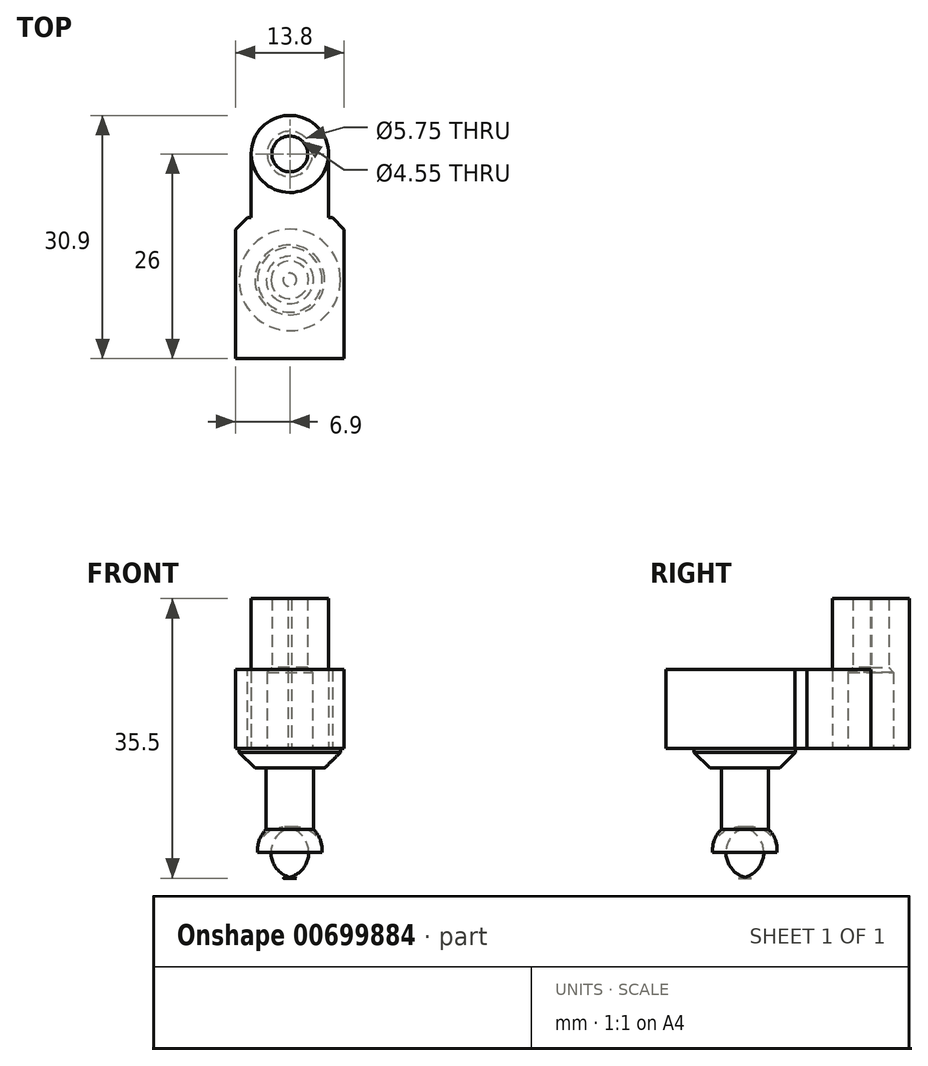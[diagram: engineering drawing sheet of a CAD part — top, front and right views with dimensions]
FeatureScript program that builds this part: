
annotation { "Feature Type Name" : "Feature", "Feature Type Description" : "" }
export const myFeature = defineFeature(function(context is Context, id is Id, definition is map)
    precondition{}
    {
        {
            var Q0;
            Q0=qCreatedBy(makeId("Top.planeOp"),FACE);
            var sketch = newSketch(context, id + "F0", { "sketchPlane" : qUnion([Q0])});
            skLineSegment(sketch, "E0.bottom", {"start": v(0, 0) * mm, "end": v(13.8, 0) * mm});
            skLineSegment(sketch, "E0.top", {"start": v(0, 17.9) * mm, "end": v(13.8, 17.9) * mm});
            skLineSegment(sketch, "E0.left", {"start": v(0, 0) * mm, "end": v(0, 17.9) * mm});
            skLineSegment(sketch, "E0.right", {"start": v(13.8, 0) * mm, "end": v(13.8, 17.9) * mm});
            skLineSegment(sketch, "E1", {"start": v(2, 17.9) * mm, "end": v(2, 26.15) * mm});
            skLineSegment(sketch, "E2", {"start": v(6.74, 30.9) * mm, "end": v(7.12, 30.9) * mm});
            skLineSegment(sketch, "E3", {"start": v(11.8, 26.21) * mm, "end": v(11.8, 17.9) * mm});
            skCircle(sketch, "E4", {"center": v(6.9, 26) * mm, "radius": 2.28 * mm});
            skCircle(sketch, "E5", {"center": v(6.9, 26) * mm, "radius": 4.9 * mm});
            skPoint(sketch, "E6.visualSharp", {"position": v(2, 30.9) * mm});
            skArc(sketch, "E6.filletArc", {"start": v(6.74, 30.9) * mm, "mid": v(3.39, 29.5) * mm, "end": v(2, 26.15) * mm});
            skPoint(sketch, "E7.visualSharp", {"position": v(11.8, 30.9) * mm});
            skArc(sketch, "E7.filletArc", {"start": v(11.8, 26.21) * mm, "mid": v(10.43, 29.52) * mm, "end": v(7.12, 30.9) * mm});
            skCircle(sketch, "E8", {"center": v(6.9, 10) * mm, "radius": 3 * mm});
            skCircle(sketch, "E9", {"center": v(6.9, 10) * mm, "radius": 4.1 * mm});
            skCircle(sketch, "E10", {"center": v(6.9, 10) * mm, "radius": 6.44 * mm});
            skCircle(sketch, "E11", {"center": v(6.9, 26) * mm, "radius": 2.88 * mm});
            skSolve(sketch);
        }
        {
            var Q0;
            {var subQ7=sQuery(id+"F0.wireOp",EDGE,"E2");Q0=makeQuery(id+"F0.imprint","IMPRINT",FACE,{"disambiguationData":[TD([[makeQuery(id+"F0.imprint","IMPRINT",EDGE,{"derivedFrom":subQ7}),-1.0]])]});}
            extrude(context, id + "F1", {"entities" : qUnion([Q0]), "depth" : 19 * mm, "offsetDistance" : 25 * mm});
        }
        {
            var Q0;
            Q0=makeQuery(id+"F0.imprint","IMPRINT",FACE,{"disambiguationData":[TD([[makeQuery(id+"F0.imprint","IMPRINT",EDGE,{"derivedFrom":sQuery(id+"F0.wireOp",EDGE,"E8")}),1.0]])]});
            extrude(context, id + "F2", {"entities" : qUnion([Q0]), "depth" : -16.5 * mm, "offsetDistance" : 25 * mm});
        }
        {
            var Q0;
            Q0=makeQuery(id+"F0.imprint","IMPRINT",FACE,{"disambiguationData":[TD([[makeQuery(id+"F0.imprint","IMPRINT",EDGE,{"derivedFrom":sQuery(id+"F0.wireOp",EDGE,"E8")}),-1.0]])]});
            extrude(context, id + "F3", {"entities" : qUnion([Q0]), "operationType" : NewBodyOperationType.ADD, "depth" : -16.5 * mm, "offsetDistance" : 25 * mm, "hasSecondDirection" : true, "secondDirectionOppositeDirection" : true, "secondDirectionDepth" : 10.3 * mm});
        }
        {
            var Q0;
            Q0=makeQuery(id+"F0.imprint","IMPRINT",FACE,{"disambiguationData":[TD([[makeQuery(id+"F0.imprint","IMPRINT",EDGE,{"derivedFrom":sQuery(id+"F0.wireOp",EDGE,"E9")}),-1.0]])]});
            var Q1;
            Q1=makeQuery(id+"F0.imprint","IMPRINT",FACE,{"disambiguationData":[TD([[makeQuery(id+"F0.imprint","IMPRINT",EDGE,{"derivedFrom":sQuery(id+"F0.wireOp",EDGE,"E8")}),-1.0]])]});
            extrude(context, id + "F4", {"entities" : qUnion([Q0, Q1]), "operationType" : NewBodyOperationType.ADD, "depth" : -2.5 * mm, "offsetDistance" : 25 * mm});
        }
        {
            var Q0;
            {var subQ0=sQuery(id+"F0.wireOp",EDGE,"E1");var subQ1=sQuery(id+"F0.wireOp",EDGE,"E0.top");var subQ2=makeQuery(id+"F0.imprint","INTERSECT",VERTEX,{"derivedFrom":[subQ1,subQ0]});Q0=makeQuery(id+"F0.imprint","IMPRINT",FACE,{"disambiguationData":[TD([[makeQuery(id+"F0.imprint","IMPRINT",EDGE,{"disambiguationData":[TD([[subQ2,-1.0]])],"derivedFrom":subQ1}),1.0]])]});}
            var Q1;
            Q1=makeQuery(id+"F0.imprint","IMPRINT",FACE,{"disambiguationData":[TD([[makeQuery(id+"F0.imprint","IMPRINT",EDGE,{"derivedFrom":sQuery(id+"F0.wireOp",EDGE,"E0.bottom")}),1.0]])]});
            var Q2;
            Q2=makeQuery(id+"F0.imprint","IMPRINT",FACE,{"disambiguationData":[TD([[makeQuery(id+"F0.imprint","IMPRINT",EDGE,{"derivedFrom":sQuery(id+"F0.wireOp",EDGE,"E9")}),-1.0]])]});
            var Q3;
            Q3=makeQuery(id+"F0.imprint","IMPRINT",FACE,{"disambiguationData":[TD([[makeQuery(id+"F0.imprint","IMPRINT",EDGE,{"derivedFrom":sQuery(id+"F0.wireOp",EDGE,"E8")}),-1.0]])]});
            var Q4;
            Q4=makeQuery(id+"F0.imprint","IMPRINT",FACE,{"disambiguationData":[TD([[makeQuery(id+"F0.imprint","IMPRINT",EDGE,{"derivedFrom":sQuery(id+"F0.wireOp",EDGE,"E8")}),1.0]])]});
            extrude(context, id + "F5", {"entities" : qUnion([Q0, Q1, Q2, Q3, Q4]), "depth" : 10 * mm, "offsetDistance" : 25 * mm});
        }
        {
            var Q0;
            Q0=makeQuery(id+"F3.opExtrude","CAP_EDGE",EDGE,{"disambiguationData":[OSD([sQuery(id+"F0.wireOp",EDGE,"E9")])],"isStart":false});
            fillet(context, id + "F6", {"entities" : qUnion([Q0]), "radius" : 3.25 * mm, "tangentPropagation" : true, "allowEdgeOverflow" : false});
        }
        {
            var Q0;
            Q0=makeQuery(id+"F3.opExtrude","CAP_EDGE",EDGE,{"disambiguationData":[OSD([sQuery(id+"F0.wireOp",EDGE,"E9")])],"isStart":true});
            fillet(context, id + "F7", {"entities" : qUnion([Q0]), "radius" : 3.6 * mm, "tangentPropagation" : true, "allowEdgeOverflow" : false});
        }
        {
            var Q0;
            Q0=makeQuery(id+"F4.opExtrude","CAP_EDGE",EDGE,{"disambiguationData":[OSD([sQuery(id+"F0.wireOp",EDGE,"E10")])],"isStart":false});
            chamfer(context, id + "F8", {"entities" : qUnion([Q0]), "width" : 2 * mm, "tangentPropagation" : true});
        }
        {
            var Q0;
            Q0=makeQuery(id+"F0.imprint","IMPRINT",FACE,{"disambiguationData":[TD([[makeQuery(id+"F0.imprint","IMPRINT",EDGE,{"derivedFrom":sQuery(id+"F0.wireOp",EDGE,"E4")}),-1.0]])]});
            extrude(context, id + "F9", {"entities" : qUnion([Q0]), "operationType" : NewBodyOperationType.ADD, "depth" : 19 * mm, "offsetDistance" : 25 * mm, "hasSecondDirection" : true, "secondDirectionOppositeDirection" : true, "secondDirectionDepth" : -9 * mm});
        }
        {
            var Q0;
            Q0=makeQuery(id+"F9.opExtrude","CAP_EDGE",EDGE,{"disambiguationData":[OSD([sQuery(id+"F0.wireOp",EDGE,"E4")])],"isStart":true});
            chamfer(context, id + "F10", {"entities" : qUnion([Q0]), "width" : 1.25 * mm, "tangentPropagation" : true});
        }
        {
            var Q0;
            Q0=makeQuery(id+"F5.opExtrude","SWEPT_EDGE",EDGE,{"disambiguationData":[OSD([sQuery(id+"F0.wireOp",EDGE,"E0.top"),sQuery(id+"F0.wireOp",EDGE,"E0.left")])]});
            var Q1;
            Q1=makeQuery(id+"F5.opExtrude","SWEPT_EDGE",EDGE,{"disambiguationData":[OSD([sQuery(id+"F0.wireOp",EDGE,"E0.top"),sQuery(id+"F0.wireOp",EDGE,"E0.right")])]});
            chamfer(context, id + "F11", {"entities" : qUnion([Q0, Q1]), "width" : 1.5 * mm, "tangentPropagation" : true});
        }
    });
